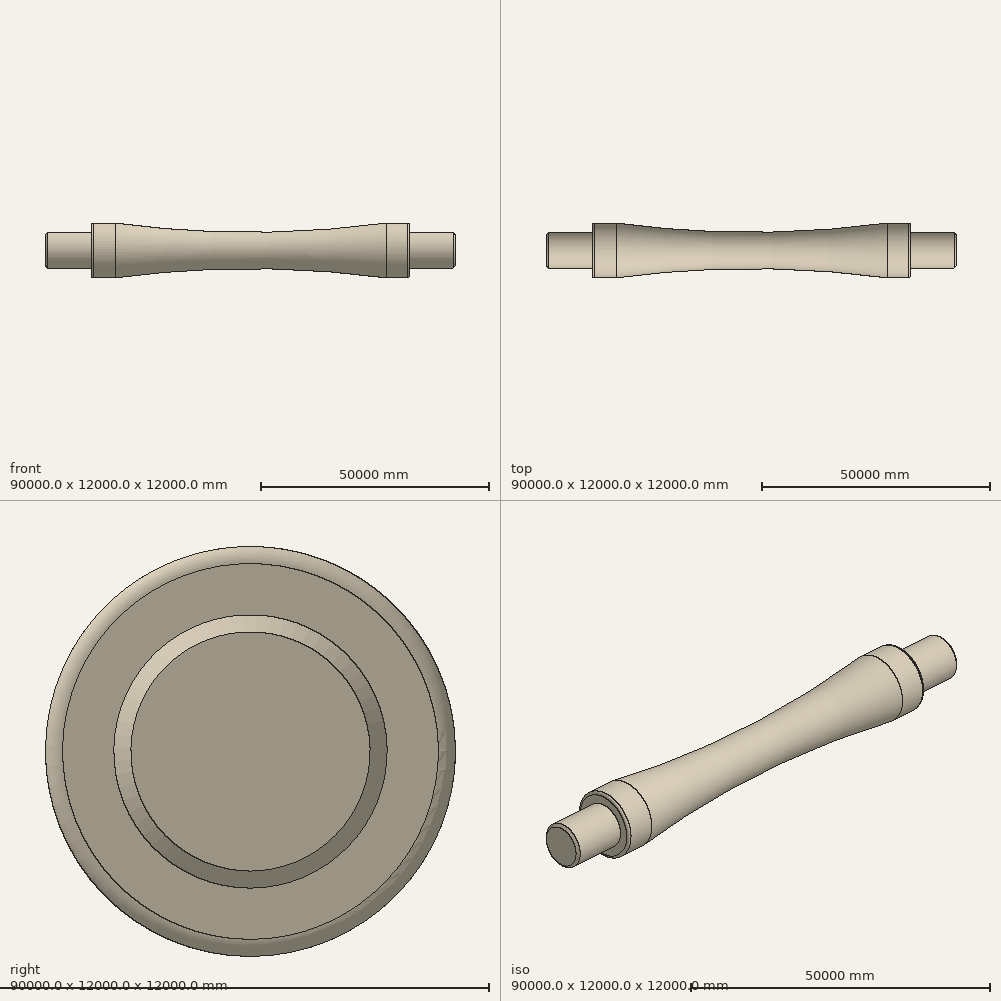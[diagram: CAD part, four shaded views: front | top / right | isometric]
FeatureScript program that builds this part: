
annotation { "Feature Type Name" : "Feature", "Feature Type Description" : "" }
export const myFeature = defineFeature(function(context is Context, id is Id, definition is map)
    precondition{}
    {
        {
            var Q0;
            Q0=qCreatedBy(makeId("Right.planeOp"),FACE);
            var sketch = newSketch(context, id + "F0", { "sketchPlane" : qUnion([Q0])});
            skCircle(sketch, "E0", {"center": v(0, 0) * mm, "radius": 4000 * mm});
            skSolve(sketch);
        }
        {
            var Q0;
            Q0=makeQuery(id+"F0.imprint","IMPRINT",FACE,{"disambiguationData":[TD([[makeQuery(id+"F0.imprint","IMPRINT",EDGE,{"derivedFrom":sQuery(id+"F0.wireOp",EDGE,"E0")}),1.0]])]});
            extrude(context, id + "F1", {"entities" : qUnion([Q0]), "depth" : 90000 * mm, "symmetric" : true});
        }
        {
            var Q0;
            Q0=qCreatedBy(makeId("Right.planeOp"),FACE);
            var sketch = newSketch(context, id + "F2", { "sketchPlane" : qUnion([Q0])});
            skCircle(sketch, "E1", {"center": v(0, 0) * mm, "radius": 6000 * mm});
            skSolve(sketch);
        }
        {
            var Q0;
            Q0=makeQuery(id+"F2.imprint","IMPRINT",FACE,{"disambiguationData":[TD([[makeQuery(id+"F2.imprint","IMPRINT",EDGE,{"derivedFrom":sQuery(id+"F2.wireOp",EDGE,"E1")}),1.0]])]});
            extrude(context, id + "F3", {"entities" : qUnion([Q0]), "operationType" : NewBodyOperationType.ADD, "depth" : 70000 * mm, "symmetric" : true});
        }
        {
            var Q0;
            Q0=qCreatedBy(makeId("Front.planeOp"),FACE);
            var sketch = newSketch(context, id + "F4", { "sketchPlane" : qUnion([Q0])});
            skLineSegment(sketch, "E2", {"start": v(-45511.41, 0) * mm, "end": v(45581.11, 0) * mm, "construction": true});
            skLineSegment(sketch, "E3", {"start": v(34917.64, 6046.05) * mm, "end": v(-34987.34, 6046.05) * mm, "construction": true});
            skSolve(sketch);
        }
        {
            var Q0;
            Q0=qCreatedBy(makeId("Front.planeOp"),FACE);
            var sketch = newSketch(context, id + "F5", { "sketchPlane" : qUnion([Q0])});
            skArc(sketch, "E4", {"start": v(-29900.79, 6046.05) * mm, "mid": v(99.21, 4000) * mm, "end": v(30099.21, 6046.05) * mm});
            skLineSegment(sketch, "E5", {"start": v(-29900.79, 6046.05) * mm, "end": v(30099.21, 6046.05) * mm});
            skSolve(sketch);
        }
        {
            var Q0;
            Q0=makeQuery(id+"F5.imprint","IMPRINT",FACE,{"disambiguationData":[TD([[makeQuery(id+"F5.imprint","IMPRINT",EDGE,{"derivedFrom":sQuery(id+"F5.wireOp",EDGE,"E4")}),1.0]])]});
            var Q1;
            Q1=sQuery(id+"F4.wireOp",EDGE,"E2");
            revolve(context, id + "F6", {"operationType" : NewBodyOperationType.REMOVE, "entities" : qUnion([Q0]), "axis" : qUnion([Q1]), "revolveType" : RevolveType.FULL, "oppositeDirection" : true});
        }
        {
            var Q0;
            Q0=makeQuery(id+"F3.opExtrude","CAP_EDGE",EDGE,{"disambiguationData":[OSD([sQuery(id+"F2.wireOp",EDGE,"E1")])],"isStart":true});
            var Q1;
            Q1=makeQuery(id+"F3.opExtrude","CAP_EDGE",EDGE,{"disambiguationData":[OSD([sQuery(id+"F2.wireOp",EDGE,"E1")])],"isStart":false});
            fillet(context, id + "F7", {"entities" : qUnion([Q0, Q1]), "radius" : 500 * mm, "tangentPropagation" : true, "allowEdgeOverflow" : false});
        }
        {
            var Q0;
            Q0=makeQuery(id+"F1.opExtrude","CAP_EDGE",EDGE,{"disambiguationData":[OSD([sQuery(id+"F0.wireOp",EDGE,"E0")])],"isStart":true});
            var Q1;
            Q1=makeQuery(id+"F1.opExtrude","CAP_EDGE",EDGE,{"disambiguationData":[OSD([sQuery(id+"F0.wireOp",EDGE,"E0")])],"isStart":false});
            chamfer(context, id + "F8", {"entities" : qUnion([Q0, Q1]), "width" : 500 * mm, "tangentPropagation" : true});
        }
    });
